# Revit family: FL -1000
name_source: partatom
category: HLS-Bauteile
revit_build: Autodesk Revit 2017 (Build: 20190507_1515(x64)
units: mm (PartAtom-declared; Revit-internal decimal feet)

## family parameters
Arbeitsebenenbasiert = Ja
Beim Laden mit Abzugskörper schneiden = Nein
Bemaßung runder Anschluss = Durchmesser verwenden
Gemeinsam genutzt = Ja
Immer vertikal = Nein
Raumberechnungspunkt = Nein
Teiletyp = Normal

## types (1)
- Federlager FL - 1000
    Anschluss = M12
    Artikelnummer = 07919010
    Breite = 78 mm  [stored 0.255906 ft]
    EAN = 4250928419019
    Fabrikat = MEFA
    Federrate = 38,61 N/mm
    Firma = MEFA Befestigungs- und Montagesysteme GmbH
    Gewicht = 3.12 kg
    Gewicht pro Bauteil = 3.12 kg
    Höhe = 83 mm
    Kurztext1 = Federlager FL Typ 1 - 1000
    Kurztext2 = F 0 - 1.023 N max. Federweg 26,5 mm
    Länge = 260 mm  [stored 0.853018 ft]
    Material = Stahl
    Materialname = S235
    Mengeneinheit = St
    Oberflaeche = galvanisch verzinkt
    Vorgabe-Ansicht = 1219 mm
    max. Federweg = 27 mm
    max. Lastbereich = 1.023 N
    min. Lastbereich = 0 N
    vpe = 1 St

note: [stored X ft] marks values corroborated as IEEE doubles in the binary element streams (Revit-internal decimal feet)
